# Revit family: Plumbing-Flushometer-Sloan-Valve-Sloan-186-ESS_
name_source: partatom
category: Plumbing Fixtures
units: mm (PartAtom-declared; Revit-internal decimal feet)

## family parameters
Cut with Voids When Loaded = No
Host = Face
OmniClass Number = 23.45.05.14.99
OmniClass Title = Other Sanitary Washing Plumbing Fixtures
Part Type = Normal
Room Calculation Point = No
Round Connector Dimension = Use Diameter
Shared = No

## types (22) — shared parameters
Apparent Load = 0 VA
Assembly Code = D2020300
CW Connection = Yes
Centerline of Supply from Top of Fixture = 11 1/2"
Centerline of Supply to Centerline of Valve = 4 3/4"
Current = 0 A
Default Elevation = 0"
Edition number = 1
HW Connection = No
Height = 14"
Keynote = 15410
Manufacturer = Sloan Valve
Number of Poles = 1
Operating Water Pressure = 15 – 80 PSI (103 – 552 kPa)
Power Factor = 1
Product Material = Sloan Valve - Finish - Polished Chrome
Product data url = https://bimobject.com
URL = www.sloanvalve.com
Valve Pressure Drop = 0.00 psi
Vent Connection = No
Voltage = 24 V
Waste Connection = No
Water Inlet Connection Diameter = 1"
zero-valued in all types: CWFU, HWFU, WFU

## per-type parameters (varying)
| type | Description | Flush Rate | Override Button | Part Number | True Mechanical Override | z_CL EL Box |
| SLOAN 186 ESS-1.0-L/STOP-HW-L-XYV | 1.0 gpf, Polished Chrome Finish, Fixture Connection Top Spud, Single Flush, Less Control Stop, Hardwired, Metal Index Push Button, SensorOperated, Less Vacuum Breaker, Sloan® Exposed Sensor Hardwired Urinal Flushometer. | 1.0 gpf (3.8 Lpf) | No | 3772676 | No | 2 1/2" |
| SLOAN 186 ESS-0.5-1-IN-STOP-OR-HW | 0.5 gpf, Polished Chrome Finish, Fixture Connection Top Spud, Single Flush, 1" Control Stop, Electrical Override, Hardwired, SensorOperated, Sloan® Exposed Sensor Hardwired Urinal Flushometer. | 0.5 gpf (1.9 Lpf) | No | 3772640 | No | 2 1/2" |
| SLOAN 186 ESS-1.5-DFB-HW | 1.5 gpf, Dual-Filtered Fixed Bypass Diaphragm, Polished Chrome Finish, Fixture Connection Top Spud, Single Flush, Hardwired, SensorOperated, Sloan® Exposed Sensor Hardwired Urinal Flushometer. | 1.5 gpf (5.7 Lpf) | No | 3772610 | No | 2 1/2" |
| SLOAN 186 ESS-1.0-HW - 3 | 1.0 gpf, Polished Chrome Finish, Fixture Connection Top Spud, Single Flush, Hardwired, Sensor-Operated, Sloan® Exposed Sensor Hardwired Urinal Flushometer. | 1.0 gpf (3.8 Lpf) | No | 3772680 | No | 2 1/2" |
| SLOAN 186 ESS-1.0-HW - 2 | 1.0 gpf, Polished Chrome Finish, Fixture Connection Top Spud, Single Flush, Hardwired, Sensor-Operated, Sloan® Exposed Sensor Hardwired Urinal Flushometer. | 1.0 gpf (3.8 Lpf) | No | 3772675 | No | 2 1/2" |
| SLOAN 186 ESS-1.0-DBP-OR-HW | 1.0 gpf, Polished Chrome Finish, Fixture Connection Top Spud, Single Flush, Hardwired, Sensor-Operated, Sloan® Exposed Sensor Hardwired Urinal Flushometer. | 1.0 gpf (3.8 Lpf) | Yes | 3772611 | No | 2 1/2" |
| SLOAN 186 ESS-0.5-HW-LL | 0.5 gpf, Polished Chrome Finish, Fixture Connection Top Spud, Single Flush, Hardwired, Sensor-Operated, Less Logo, Sloan® Exposed Sensor Hardwired Urinal Flushometer. | 0.5 gpf (1.9 Lpf) | No | 3772628 | No | 2 1/2" |
| SLOAN 186 ESS-0.25-DBP-OR-HW | 0.25 gpf, Dual-Filtered Bypass, Polished Chrome Finish, Fixture Connection Top Spud, Single Flush, Electrical Override, Hardwired, Sensor-Operated, Sloan® Exposed Sensor Hardwired Urinal Flushometer. | 0.25 gpf (0.9 Lpf) | Yes | 3772622 | No | 2 1/2" |
| SLOAN 186 ESS-0.25-DBP-HW | 0.25 gpf, Dual-Filtered Bypass, Polished Chrome Finish, Fixture Connection Top Spud, Single Flush, Hardwired, Sensor-Operated, Sloan® Exposed Sensor Hardwired Urinal Flushometer. | 0.25 gpf (0.9 Lpf) | No | 3772684 | No | 2 1/2" |
| SLOAN 186 ESS-1.5-HW | 1.5 gpf, Polished Chrome Finish, Fixture Connection Top Spud, Single Flush, Hardwired, Sensor-Operated, Sloan® Exposed Sensor Hardwired Urinal Flushometer. | 1.5 gpf (5.7 Lpf) | No | 3772600 | No | 2 1/2" |
| SLOAN 186 ESS-0.5-OR-HW | 0.5 gpf, Polished Chrome Finish, Fixture Connection Top Spud, Single Flush, Electrical Override, Hardwired, Sensor-Operated, Sloan® Exposed Sensor Hardwired Urinal Flushometer. | 0.5 gpf (1.9 Lpf) | No | 3772604 | No | 2 1/2" |
| SLOAN 186 ESS-0.5-DFB-OR-HW | 0.5 gpf, Dual-Filtered Fixed Bypass Diaphragm, Polished Chrome Finish, Fixture Connection Top Spud, Single Flush, Electrical Override, Hardwired, Sensor-Operated, Sloan® Exposed Sensor Hardwired Urinal Flushometer. | 0.5 gpf (1.9 Lpf) | No | 3772620 | No | 2 1/2" |
| SLOAN 186 ESS-0.5-TMO-HW | 0.5 gpf, Polished Chrome Finish, Fixture Connection Top Spud, Single Flush, True Mechanical Override, Hardwired, Sensor-Operated, Sloan® Exposed Sensor Hardwired Urinal Flushometer. | 0.5 gpf (1.9 Lpf) | No | 3772649 | Yes | 6" |
| SLOAN 186 ESS-0.125-DBP-OR-HW | 0.125 gpf, Dual-Filtered Bypass, Polished Chrome Finish, Fixture Connection Top Spud, Single Flush, Electrical Override, Hardwired, Sensor-Operated, Sloan® Exposed Sensor Hardwired Urinal Flushometer. | 0.125 gpf (0.5 Lpf) | Yes | 3772647 | No | 2 1/2" |
| SLOAN 186 ESS-1.0-DFB-TMO-HW | 1.0 gpf, Dual-Filtered Fixed Bypass Diaphragm, Polished Chrome Finish, Fixture Connection Top Spud, Single Flush, True Mechanical Override, Hardwired, Sensor-Operated, Sloan® Exposed Sensor Hardwired Urinal Flushometer. | 1.0 gpf (3.8 Lpf) | No | 3772648 | Yes | 6" |
| SLOAN 186 ESS-1.0-DFB-HW | 1.0 gpf, Dual-Filtered Fixed Bypass Diaphragm, Polished Chrome Finish, Fixture Connection Top Spud, Single Flush, Hardwired, SensorOperated, Sloan® Exposed Sensor Hardwired Urinal Flushometer. | 1.0 gpf (3.8 Lpf) | No | 3772683 | No | 2 1/2" |
| SLOAN 186 ESS-0.5-DFB-TMO-HW | 0.5 gpf, Dual-Filtered Fixed Bypass Diaphragm, Polished Chrome Finish, Fixture Connection Top Spud, Single Flush, True Mechanical Override, Hardwired, Sensor-Operated, Sloan® Exposed Sensor Hardwired Urinal Flushometer. | 0.5 gpf (1.9 Lpf) | No | 3772646 | Yes | 6" |
| SLOAN 186 ESS-0.5-DFB-HW | 0.5 gpf, Dual-Filtered Fixed Bypass Diaphragm, Polished Chrome Finish, Fixture Connection Top Spud, Single Flush, Hardwired, SensorOperated, Sloan® Exposed Sensor Hardwired Urinal Flushometer. | 0.5 gpf (1.9 Lpf) | No | 3772613 | No | 2 1/2" |
| SLOAN 186 ESS-0.5-HW | 0.5 gpf, Polished Chrome Finish, Fixture Connection Top Spud, Single Flush, Hardwired, Sensor-Operated, Sloan® Exposed Sensor Hardwired Urinal Flushometer. | 0.5 gpf (1.9 Lpf) | No | 3772603 | No | 2 1/2" |
| SLOAN 186 ESS-1.0-HW - 1 | 1.0 gpf, Polished Chrome Finish, Fixture Connection Top Spud, Single Flush, Hardwired, Sensor-Operated, Sloan® Exposed Sensor Hardwired Urinal Flushometer. | 1.0 gpf (3.8 Lpf) | No | 3772673 | No | 2 1/2" |
| SLOAN 186 ESS-0.125-DBP-TMO-HW | 0.125 gpf, Dual-Filtered Bypass, Polished Chrome Finish, Fixture Connection Top Spud, Single Flush, True Mechanical Override, Hardwired, Sensor-Operated, Sloan® Exposed Sensor Hardwired Urinal Flushometer. | 0.125 gpf (0.5 Lpf) | No | 3772645 | Yes | 6" |
| SLOAN 186 ESS-0.125-DBP-HW | 0.125 gpf, Dual-Filtered Bypass, Polished Chrome Finish, Fixture Connection Top Spud, Single Flush, Hardwired, Sensor-Operated, Sloan® Exposed Sensor Hardwired Urinal Flushometer. | 0.125 gpf (0.5 Lpf) | No | 3772695 | No | 2 1/2" |

note: column(s) folded — value = type name in every type: Model

## geometry (parser evidence)
native form markers: Sweep x9
no freeform markers — native parametric forms only
